# Revit family: SU-800-G_GENERADO
name_source: partatom
category: Equipos mecánicos
revit_build: Autodesk Revit 2014 (Build: 20130308_1515(x64)
units: mm (PartAtom-declared; Revit-internal decimal feet)

## types (38) — shared parameters
Depth = 757 mm  [stored 2.4836 ft]
Fabricante = SAMMIC S.L.
Foodservice Equipment Identifier = Sí
Height = 998 mm  [stored 3.27428 ft]
Revision Code = 1
URL = https://www.sammic.com
URL Cutsheet = http://www.sammic.com
Width = 960 mm  [stored 3.14961 ft]

## per-type parameters (varying)
| type | Comentarios de tipo | Cycle | FL Amps | HP | Modelo | Specification by Manufacturer | Volts | Watts | Weight in Pounds |
| Vacuum packing machine SU-806G 230-400/50/3N | Floorstanding unit. 63 m³/h. 530+848 mm.

ELECTRICAL DATA:

230V/50Hz/3~ (9.5A) | 50 Hz | 6 A | 4.02 | 1140883 | Two sealing bars (530+848 mm.)
63 m³/h Busch vacuum pump.
Vacuum controlled by sensor. | 400 V | 3000 W | 511.5 |
| Vacuum packing machine SU-806GP 230-400/50/3N | Floorstanding unit. 63 m³/h. 530+848 mm.

ELECTRICAL DATA:

230V/50Hz/3~ (9.5A) | 50 Hz | 6 A | 4.02 | 1140885 | Two sealing bars (530+848 mm.)
63 m³/h Busch vacuum pump.
Vacuum controlled by sensor. | 400 V | 3000 W | 511.5 |
| Vacuum packing machine SU-806G 208-240/60/3 | Floorstanding unit. 63 m³/h. 530+848 mm.

ELECTRICAL DATA:

230V/60Hz/3~ (8.2A) | 60 Hz | 8 A | 5.23 | 1140901 | Two sealing bars (530+848 mm.)
63 m³/h Busch vacuum pump.
Vacuum controlled by sensor. | 208 V | 3900 W | 511.5 |
| Vacuum packing machine SU-806GP 208-240/60/3 | Floorstanding unit. 63 m³/h. 530+848 mm.

ELECTRICAL DATA:

230V/60Hz/3~ (8.2A) | 60 Hz | 8 A | 5.23 | 1140903 | Two sealing bars (530+848 mm.)
63 m³/h Busch vacuum pump.
Vacuum controlled by sensor. | 208 V | 3900 W | 511.5 |
| Vacuum packing machine SU-806G CC 230-400/50/3N | Floorstanding unit. 63 m³/h. 581+581 mm.

ELECTRICAL DATA:

230V/50Hz/3~ (9.5A) | 50 Hz | 6 A | 3.62 | 1140889 | Two sealing bars (581+581 mm.)
63 m³/h Busch vacuum pump.
Vacuum controlled by sensor. | 400 V | 2700 W | 511.5 |
| Vacuum packing machine SU-806GP CC 230-400/50/3N | Floorstanding unit. 63 m³/h. 581+581 mm.

ELECTRICAL DATA:

230V/50Hz/3~ (9.5A) | 50 Hz | 6 A | 3.62 | 1140891 | Two sealing bars (581+581 mm.)
63 m³/h Busch vacuum pump.
Vacuum controlled by sensor. | 400 V | 2700 W | 511.5 |
| Vacuum packing machine SU-806G CC 208-240/60/3 | Floorstanding unit. 63 m³/h. 581+581 mm.

ELECTRICAL DATA:

230V/60Hz/3~ (8.2A) | 60 Hz | 8 A | 4.83 | 1140907 | Two sealing bars (581+581 mm.)
63 m³/h Busch vacuum pump.
Vacuum controlled by sensor. | 208 V | 3600 W | 511.5 |
| Vacuum packing machine SU-806GP CC 208-240/60/3 | Floorstanding unit. 63 m³/h. 581+581 mm.

ELECTRICAL DATA:

230V/60Hz/3~ (8.2A) | 60 Hz | 8 A | 4.83 | 1140909 | Two sealing bars (581+581 mm.)
63 m³/h Busch vacuum pump.
Vacuum controlled by sensor. | 208 V | 3600 W | 511.5 |
| Vacuum packing machine SU-806G LL 230-400/50/3N | Floorstanding unit. 63 m³/h. 848+848 mm.

ELECTRICAL DATA:

230V/50Hz/3~ (9.5A) | 50 Hz | 6 A | 4.43 | 1140895 | Two sealing bars (848+848 mm)
63 m³/h Busch vacuum pump.
Vacuum controlled by sensor. | 400 V | 3300 W | 511.5 |
| Vacuum packing machine SU-806GP LL 230-400/50/3N | Floorstanding unit. 63 m³/h. 848+848 mm.

ELECTRICAL DATA:

230V/50Hz/3~ (9.5A) | 50 Hz | 6 A | 4.43 | 1140897 | Two sealing bars (848+848 mm)
63 m³/h Busch vacuum pump.
Vacuum controlled by sensor. | 400 V | 3300 W | 511.5 |
| Vacuum packing machine SU-806G LL 208-240/60/3 | Floorstanding unit. 63 m³/h. 848+848 mm.

ELECTRICAL DATA:

230V/60Hz/3~ (8.2A) | 60 Hz | 8 A | 5.63 | 1140913 | Two sealing bars (848+848 mm)
63 m³/h Busch vacuum pump.
Vacuum controlled by sensor. | 208 V | 4200 W | 511.5 |
| Vacuum packing machine SU-806GP LL 208-240/60/3 | Floorstanding unit. 63 m³/h. 848+848 mm.

ELECTRICAL DATA:

230V/60Hz/3~ (8.2A) | 60 Hz | 8 A | 5.63 | 1140915 | Two sealing bars (848+848 mm)
63 m³/h Busch vacuum pump.
Vacuum controlled by sensor. | 208 V | 4200 W | 511.5 |
| Vacuum packing machine SU-806GP LL 220/60/3 | Floorstanding unit. 63 m³/h. 848+848 mm.

ELECTRICAL DATA:

380V/60Hz/3N~ (4.4A) | 60 Hz | 10 A | 4.43 | 1140933 | Two sealing bars (848+848 mm)
63 m³/h Busch vacuum pump.
Vacuum controlled by sensor. | 220 V | 3300 W | 511.5 |
| Vacuum packing machine SU-806GP LL 230/50-60/1 | Floorstanding unit. 63 m³/h. 848+848 mm.

ELECTRICAL DATA:

230V/50Hz/3~ (9.5A) | 50 Hz | 6 A | 4.43 | 1140898 | Two sealing bars (848+848 mm)
63 m³/h Busch vacuum pump.
Vacuum controlled by sensor. | 400 V | 3300 W | 511.5 |
| Vacuum packing machine SU-810G 400/50-60/3N | Floorstanding unit. 100m³/h. 530+848 mm. | 50 Hz | 8 A | 4.96 | 1140937 | Two sealing bars (530+848 mm.)
100 m³/h Busch vacuum pump.
Vacuum controlled by sensor. | 400 V | 3700 W | 551.2 |
| Vacuum packing machine SU-810GP 400/50-60/3N | Floorstanding unit. 100m³/h. 530+848 mm. | 50 Hz | 8 A | 4.96 | 1140941 | Two sealing bars (530+848 mm.)
100 m³/h Busch vacuum pump.
Vacuum controlled by sensor. | 400 V | 3700 W | 551.2 |
| Vacuum packing machine SU-810G+ 400/50-60/3N | Floorstanding unit. 100m³/h. 530+848 mm. | 50 Hz | 8 A | 4.96 | 1140942 | Two sealing bars (530+848 mm.)
100 m³/h Busch vacuum pump.
Vacuum controlled by sensor. | 400 V | 3700 W | 551.2 |
| Vacuum packing machine SU-810GP+ 400/50-60/3N | Floorstanding unit. 100m³/h. 530+848 mm. | 50 Hz | 8 A | 4.96 | 1140943 | Two sealing bars (530+848 mm.)
100 m³/h Busch vacuum pump.
Vacuum controlled by sensor. | 400 V | 3700 W | 551.2 |
| Vacuum packing machine SU-810G 208-240/60/3 | Floorstanding unit. 100m³/h. 530+848 mm.

ELECTRICAL DATA:

230V/60Hz/3~ (12.8A) | 60 Hz | 13 A | 6.57 | 1140967 | Two sealing bars (530+848 mm.)
100 m³/h Busch vacuum pump.
Vacuum controlled by sensor. | 208 V | 4900 W | 551.2 |
| Vacuum packing machine SU-810GP 208-240/60/3 | Floorstanding unit. 100m³/h. 530+848 mm.

ELECTRICAL DATA:

230V/60Hz/3~ (12.8A) | 60 Hz | 13 A | 6.57 | 1140971 | Two sealing bars (530+848 mm.)
100 m³/h Busch vacuum pump.
Vacuum controlled by sensor. | 208 V | 4900 W | 551.2 |
| Vacuum packing machine SU-810G+ 208-240/60/3 | Floorstanding unit. 100m³/h. 530+848 mm.

ELECTRICAL DATA:

230V/60Hz/3~ (12.8A) | 60 Hz | 13 A | 6.57 | 1140972 | Two sealing bars (530+848 mm.)
100 m³/h Busch vacuum pump.
Vacuum controlled by sensor. | 208 V | 4900 W | 551.2 |
| Vacuum packing machine SU-810GP+ 208-240/60/3 | Floorstanding unit. 100m³/h. 530+848 mm.

ELECTRICAL DATA:

230V/60Hz/3~ (12.8A) | 60 Hz | 13 A | 6.57 | 1140973 | Two sealing bars (530+848 mm.)
100 m³/h Busch vacuum pump.
Vacuum controlled by sensor. | 208 V | 4900 W | 551.2 |
| Vacuum packing machine SU-810GP+ 220/60/3 | Floorstanding unit. 100m³/h. 530+848 mm. | 60 Hz | 15 A | 6.57 | 1141004 | Two sealing bars (530+848 mm.)
100 m³/h Busch vacuum pump.
Vacuum controlled by sensor. | 220 V | 4900 W | 551.2 |
| Vacuum packing machine SU-810G CC 400/50-60/3N | Floorstanding unit. 100m³/h. 581+581 mm. | 50 Hz | 8 A | 4.56 | 1140947 | Two sealing bars (581+581 mm.)
100 m³/h Busch vacuum pump.
Vacuum controlled by sensor. | 400 V | 3400 W | 551.2 |
| Vacuum packing machine SU-810GP CC 400/50-60/3N | Floorstanding unit. 100m³/h. 581+581 mm. | 50 Hz | 8 A | 4.56 | 1140951 | Two sealing bars (581+581 mm.)
100 m³/h Busch vacuum pump.
Vacuum controlled by sensor. | 400 V | 3400 W | 551.2 |
| Vacuum packing machine SU-810GP+ CC 400/50-60/3N | Floorstanding unit. 100m³/h. 581+581 mm. | 50 Hz | 8 A | 4.56 | 1140953 | Two sealing bars (581+581 mm.)
100 m³/h Busch vacuum pump.
Vacuum controlled by sensor. | 400 V | 3400 W | 551.2 |
| Vacuum packing machine SU-810G CC 208-240/60/3 | Floorstanding unit. 100m³/h. 581+581 mm.

ELECTRICAL DATA:

230V/60Hz/3~ (12.8A) | 60 Hz | 13 A | 6.17 | 1140977 | Two sealing bars (581+581 mm.)
100 m³/h Busch vacuum pump.
Vacuum controlled by sensor. | 208 V | 4600 W | 551.2 |
| Vacuum packing machine SU-810GP CC 208-240/60/3 | Floorstanding unit. 100m³/h. 581+581 mm.

ELECTRICAL DATA:

230V/60Hz/3~ (12.8A) | 60 Hz | 13 A | 6.17 | 1140981 | Two sealing bars (581+581 mm.)
100 m³/h Busch vacuum pump.
Vacuum controlled by sensor. | 208 V | 4600 W | 551.2 |
| Vacuum packing machine SU-810G+ CC 208-240/60/3 | Floorstanding unit. 100m³/h. 581+581 mm.

ELECTRICAL DATA:

230V/60Hz/3~ (12.8A) | 60 Hz | 13 A | 6.17 | 1140982 | Two sealing bars (581+581 mm.)
100 m³/h Busch vacuum pump.
Vacuum controlled by sensor. | 208 V | 4600 W | 551.2 |
| Vacuum packing machine SU-810GP+ CC 208-240/60/3 | Floorstanding unit. 100m³/h. 581+581 mm.

ELECTRICAL DATA:

230V/60Hz/3~ (12.8A) | 60 Hz | 13 A | 6.17 | 1140983 | Two sealing bars (581+581 mm.)
100 m³/h Busch vacuum pump.
Vacuum controlled by sensor. | 208 V | 4600 W | 551.2 |
| Vacuum packing machine SU-810G LL 400/50-60/3N | Floorstanding unit. 100m³/h. 848+848 mm. | 50 Hz | 8 A | 5.36 | 1140957 | Two sealing bars (848+848 mm.)
100 m³/h Busch vacuum pump.
Vacuum controlled by sensor. | 400 V | 4000 W | 551.2 |
| Vacuum packing machine SU-810GP LL 400/50-60/3N | Floorstanding unit. 100m³/h. 848+848 mm. | 50 Hz | 8 A | 5.36 | 1140961 | Two sealing bars (848+848 mm.)
100 m³/h Busch vacuum pump.
Vacuum controlled by sensor. | 400 V | 4000 W | 551.2 |
| Vacuum packing machine SU-810G+ LL 400/50-60/3N | Floorstanding unit. 100m³/h. 848+848 mm. | 50 Hz | 8 A | 5.36 | 1140962 | Two sealing bars (848+848 mm.)
100 m³/h Busch vacuum pump.
Vacuum controlled by sensor. | 400 V | 4000 W | 551.2 |
| Vacuum packing machine SU-810GP+ LL 400/50-60/3N | Floorstanding unit. 100m³/h. 848+848 mm. | 50 Hz | 8 A | 5.36 | 1140963 | Two sealing bars (848+848 mm.)
100 m³/h Busch vacuum pump.
Vacuum controlled by sensor. | 400 V | 4000 W | 551.2 |
| Vacuum packing machine SU-810G LL 208-240/60/3 | Floorstanding unit. 100m³/h. 848+848 mm.

ELECTRICAL DATA:

230V/60Hz/3~ (12.8A) | 60 Hz | 13 A | 6.97 | 1140987 | Two sealing bars (848+848 mm.)
100 m³/h Busch vacuum pump.
Vacuum controlled by sensor. | 208 V | 5200 W | 551.2 |
| Vacuum packing machine SU-810GP LL 208-240/60/3 | Floorstanding unit. 100m³/h. 848+848 mm.

ELECTRICAL DATA:

230V/60Hz/3~ (12.8A) | 60 Hz | 13 A | 6.97 | 1140991 | Two sealing bars (848+848 mm.)
100 m³/h Busch vacuum pump.
Vacuum controlled by sensor. | 208 V | 5200 W | 551.2 |
| Vacuum packing machine SU-810G+ LL 208-240/60/3 | Floorstanding unit. 100m³/h. 848+848 mm.

ELECTRICAL DATA:

230V/60Hz/3~ (12.8A) | 60 Hz | 13 A | 6.97 | 1140992 | Two sealing bars (848+848 mm.)
100 m³/h Busch vacuum pump.
Vacuum controlled by sensor. | 208 V | 5200 W | 551.2 |
| Vacuum packing machine SU-810GP+ LL 208-240/60/3 | Floorstanding unit. 100m³/h. 848+848 mm.

ELECTRICAL DATA:

230V/60Hz/3~ (12.8A) | 60 Hz | 13 A | 6.97 | 1140993 | Two sealing bars (848+848 mm.)
100 m³/h Busch vacuum pump.
Vacuum controlled by sensor. | 208 V | 5200 W | 551.2 |

note: column(s) folded — value = type name in every type: Descripción

note: [stored X ft] marks values corroborated as IEEE doubles in the binary element streams (Revit-internal decimal feet)

## geometry (parser evidence)
native form markers: Sweep x3
no freeform markers — native parametric forms only
